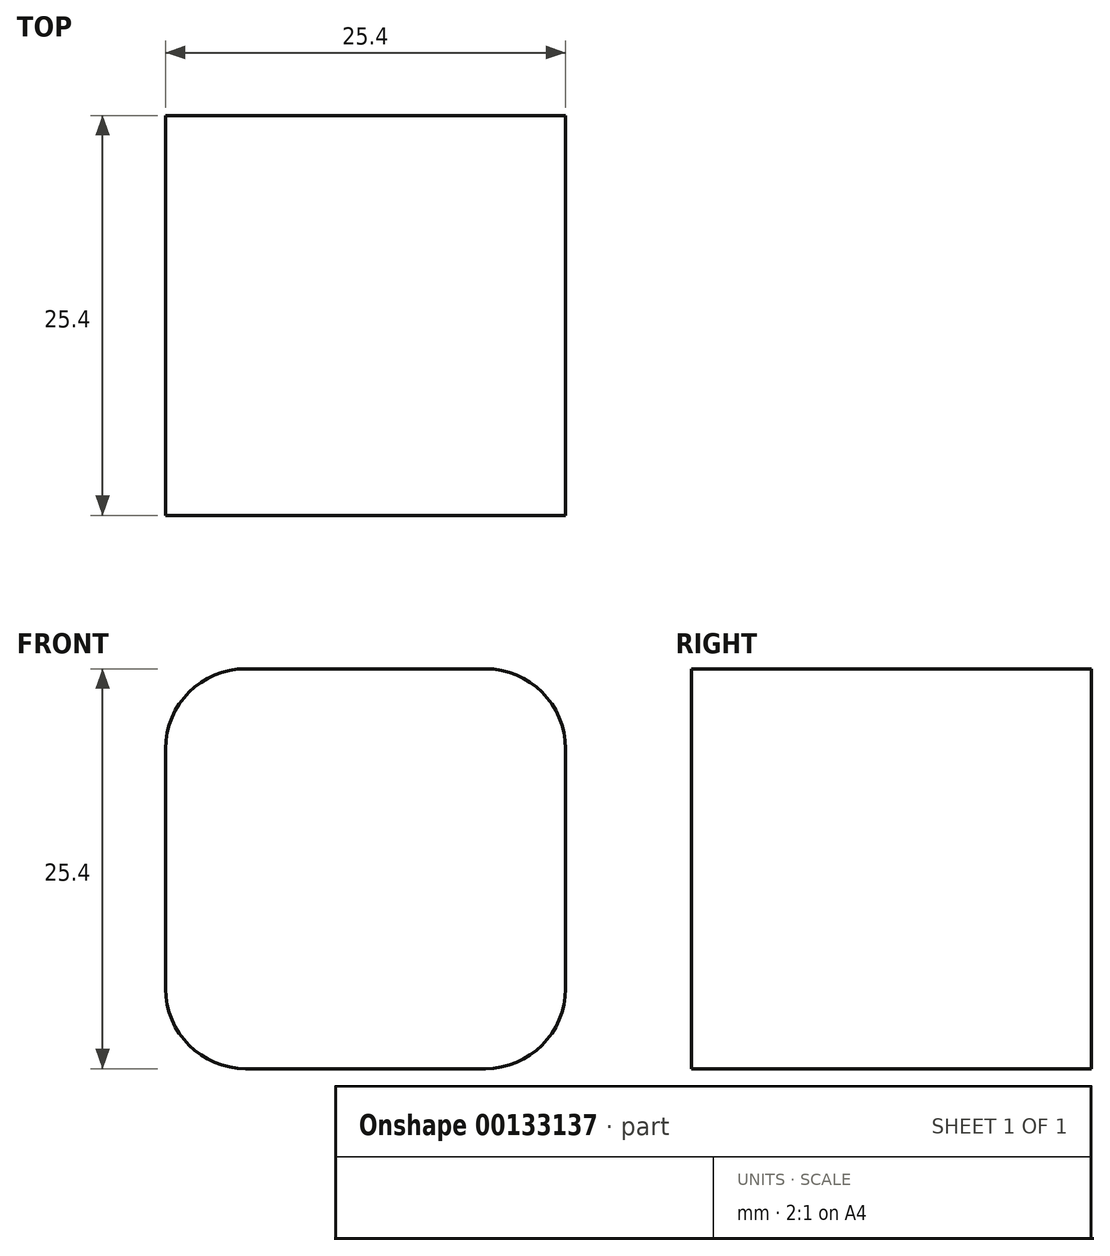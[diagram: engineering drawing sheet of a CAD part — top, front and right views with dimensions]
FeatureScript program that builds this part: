
annotation { "Feature Type Name" : "Feature", "Feature Type Description" : "" }
export const myFeature = defineFeature(function(context is Context, id is Id, definition is map)
    precondition{}
    {
        {
            var Q0;
            Q0=qCreatedBy(makeId("Front.planeOp"),FACE);
            var sketch = newSketch(context, id + "F0", { "sketchPlane" : qUnion([Q0])});
            skLineSegment(sketch, "E0.bottom", {"start": v(7.62, 12.7) * mm, "end": v(-7.62, 12.7) * mm});
            skLineSegment(sketch, "E0.top", {"start": v(7.62, -12.7) * mm, "end": v(-7.62, -12.7) * mm});
            skLineSegment(sketch, "E0.left", {"start": v(12.7, 7.62) * mm, "end": v(12.7, -7.62) * mm});
            skLineSegment(sketch, "E0.right", {"start": v(-12.7, 7.62) * mm, "end": v(-12.7, -7.62) * mm});
            skPoint(sketch, "E0.middle", {"position": v(0, 0) * mm});
            skPoint(sketch, "E1.visualSharp", {"position": v(-12.7, 12.7) * mm});
            skArc(sketch, "E1.filletArc", {"start": v(-7.62, 12.7) * mm, "mid": v(-11.21, 11.21) * mm, "end": v(-12.7, 7.62) * mm});
            skPoint(sketch, "E2.visualSharp", {"position": v(12.7, 12.7) * mm});
            skArc(sketch, "E2.filletArc", {"start": v(12.7, 7.62) * mm, "mid": v(11.21, 11.21) * mm, "end": v(7.62, 12.7) * mm});
            skPoint(sketch, "E3.visualSharp", {"position": v(12.7, -12.7) * mm});
            skArc(sketch, "E3.filletArc", {"start": v(7.62, -12.7) * mm, "mid": v(11.21, -11.21) * mm, "end": v(12.7, -7.62) * mm});
            skPoint(sketch, "E4.visualSharp", {"position": v(-12.7, -12.7) * mm});
            skArc(sketch, "E4.filletArc", {"start": v(-12.7, -7.62) * mm, "mid": v(-11.21, -11.21) * mm, "end": v(-7.62, -12.7) * mm});
            skSolve(sketch);
        }
        {
            var Q0;
            Q0=makeQuery(id+"F0.imprint","IMPRINT",FACE,{"disambiguationData":[TD([[makeQuery(id+"F0.imprint","IMPRINT",EDGE,{"derivedFrom":sQuery(id+"F0.wireOp",EDGE,"E0.bottom")}),1.0]])]});
            extrude(context, id + "F1", {"entities" : qUnion([Q0]), "depth" : 25.4 * mm});
        }
    });
